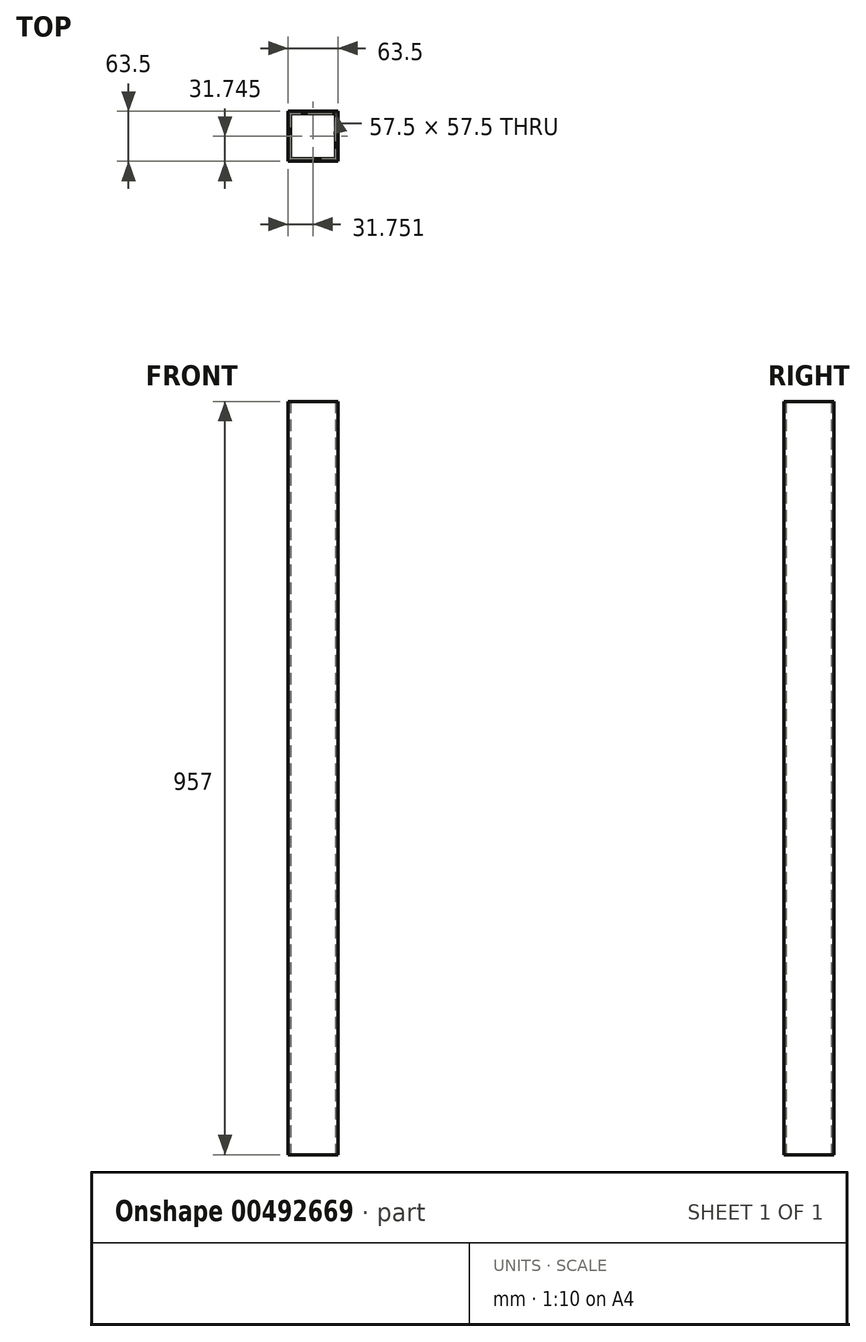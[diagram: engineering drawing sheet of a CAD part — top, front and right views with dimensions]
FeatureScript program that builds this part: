
annotation { "Feature Type Name" : "Feature", "Feature Type Description" : "" }
export const myFeature = defineFeature(function(context is Context, id is Id, definition is map)
    precondition{}
    {
        {
            var Q0;
            Q0=qCreatedBy(makeId("Top.planeOp"),FACE);
            var sketch = newSketch(context, id + "F0", { "sketchPlane" : qUnion([Q0])});
            skLineSegment(sketch, "E0.bottom", {"start": v(-18.8, 23) * mm, "end": v(38.7, 23) * mm});
            skLineSegment(sketch, "E0.top", {"start": v(-18.8, -34.5) * mm, "end": v(38.7, -34.5) * mm});
            skLineSegment(sketch, "E0.left", {"start": v(-18.8, 23) * mm, "end": v(-18.8, -34.5) * mm});
            skLineSegment(sketch, "E0.right", {"start": v(38.7, 23) * mm, "end": v(38.7, -34.5) * mm});
            skLineSegment(sketch, "E1.bottom", {"start": v(-21.8, 26) * mm, "end": v(41.7, 26) * mm});
            skLineSegment(sketch, "E1.top", {"start": v(-21.8, -37.5) * mm, "end": v(41.7, -37.5) * mm});
            skLineSegment(sketch, "E1.left", {"start": v(-21.8, 26) * mm, "end": v(-21.8, -37.5) * mm});
            skLineSegment(sketch, "E1.right", {"start": v(41.7, 26) * mm, "end": v(41.7, -37.5) * mm});
            skSolve(sketch);
        }
        {
            var Q0;
            Q0 = qSketchRegion(id + "F0", true);
            extrude(context, id + "F1", {"entities" : qUnion([Q0]), "flatOperationType" : FlatOperationType.REMOVE, "offsetDistance" : 25 * mm, "depth" : 957 * mm, "domain" : OperationDomain.MODEL});
        }
    });
